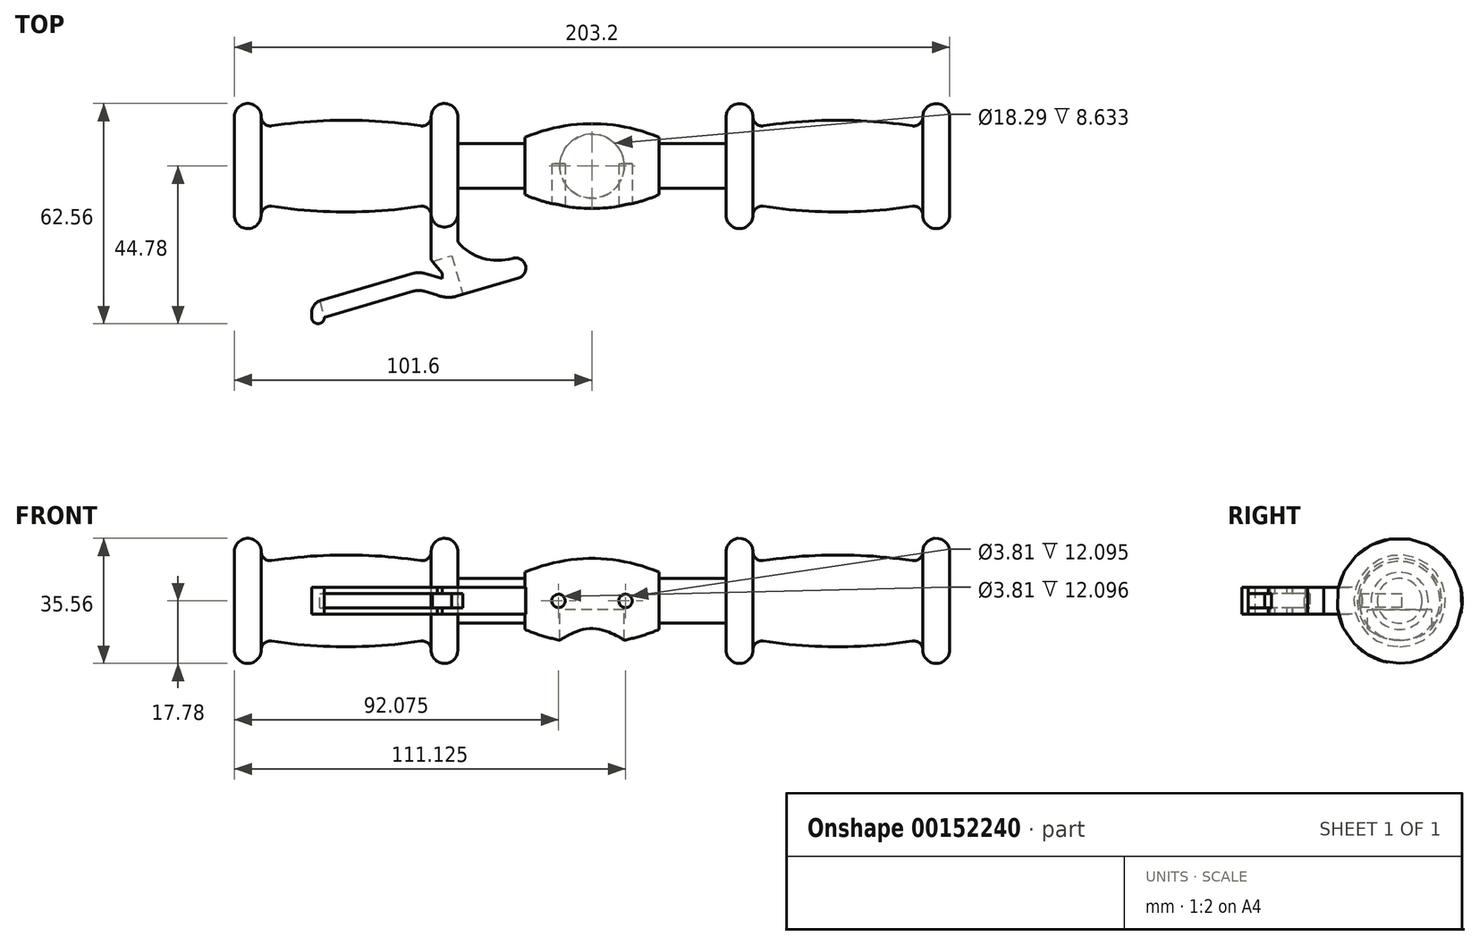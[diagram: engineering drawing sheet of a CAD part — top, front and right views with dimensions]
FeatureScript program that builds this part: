
annotation { "Feature Type Name" : "Feature", "Feature Type Description" : "" }
export const myFeature = defineFeature(function(context is Context, id is Id, definition is map)
    precondition{}
    {
        {
            var Q0;
            Q0=qCreatedBy(makeId("Right.planeOp"),FACE);
            var sketch = newSketch(context, id + "F0", { "sketchPlane" : qUnion([Q0])});
            skCircle(sketch, "E0", {"center": v(0, 0) * mm, "radius": 6.35 * mm});
            skSolve(sketch);
        }
        {
            var Q0;
            Q0 = qSketchRegion(id + "F0", true);
            extrude(context, id + "F1", {"entities" : qUnion([Q0]), "depth" : 203.2 * mm});
        }
        {
            var Q0;
            Q0=qCreatedBy(makeId("Front.planeOp"),FACE);
            var sketch = newSketch(context, id + "F2", { "sketchPlane" : qUnion([Q0])});
            skLineSegment(sketch, "E1", {"start": v(0, 6.35) * mm, "end": v(203.2, 6.35) * mm, "construction": true});
            skLineSegment(sketch, "E2", {"start": v(139.7, 6.35) * mm, "end": v(139.7, 13.97) * mm});
            skArc(sketch, "E3", {"start": v(147.32, 13.97) * mm, "mid": v(143.51, 17.78) * mm, "end": v(139.7, 13.97) * mm});
            skArc(sketch, "E4", {"start": v(147.32, 13.97) * mm, "mid": v(148.22, 12.02) * mm, "end": v(150.28, 11.43) * mm});
            skLineSegment(sketch, "E5", {"start": v(203.2, 6.35) * mm, "end": v(203.2, 13.97) * mm});
            skArc(sketch, "E6", {"start": v(203.2, 13.97) * mm, "mid": v(199.4, 17.78) * mm, "end": v(195.58, 13.97) * mm});
            skArc(sketch, "E7", {"start": v(195.58, 13.97) * mm, "mid": v(194.68, 12.02) * mm, "end": v(192.62, 11.43) * mm});
            skLineSegment(sketch, "E8", {"start": v(139.7, 6.35) * mm, "end": v(203.2, 6.35) * mm});
            skArc(sketch, "E9", {"start": v(192.62, 11.43) * mm, "mid": v(171.45, 13.04) * mm, "end": v(150.28, 11.43) * mm});
            skLineSegment(sketch, "E10", {"start": v(0, 6.35) * mm, "end": v(0, 13.97) * mm});
            skArc(sketch, "E11", {"start": v(7.62, 13.97) * mm, "mid": v(3.81, 17.78) * mm, "end": v(0, 13.97) * mm});
            skArc(sketch, "E12", {"start": v(7.62, 13.97) * mm, "mid": v(8.52, 12.02) * mm, "end": v(10.58, 11.43) * mm});
            skLineSegment(sketch, "E13", {"start": v(63.5, 6.35) * mm, "end": v(63.5, 13.97) * mm});
            skArc(sketch, "E14", {"start": v(63.5, 13.97) * mm, "mid": v(59.7, 17.78) * mm, "end": v(55.88, 13.97) * mm});
            skArc(sketch, "E15", {"start": v(55.88, 13.97) * mm, "mid": v(54.98, 12.02) * mm, "end": v(52.92, 11.43) * mm});
            skLineSegment(sketch, "E16", {"start": v(0, 6.35) * mm, "end": v(78.18, 6.35) * mm});
            skArc(sketch, "E17", {"start": v(52.92, 11.43) * mm, "mid": v(31.75, 13.04) * mm, "end": v(10.58, 11.43) * mm});
            skPoint(sketch, "E18", {"position": v(0, 6.35) * mm});
            skPoint(sketch, "E19", {"position": v(143.51, 17.78) * mm});
            skSolve(sketch);
        }
        {
            var Q0;
            Q0 = qSketchRegion(id + "F2", true);
            var Q1;
            Q1=makeQuery(id+"F1.opExtrude","SWEPT_FACE",FACE,{"disambiguationData":[OSD([sQuery(id+"F0.wireOp",EDGE,"E0")])]});
            revolve(context, id + "F3", {"operationType" : NewBodyOperationType.ADD, "entities" : qUnion([Q0]), "axis" : qUnion([Q1]), "revolveType" : RevolveType.FULL});
        }
        {
            var Q0;
            Q0=qCreatedBy(makeId("Front.planeOp"),FACE);
            var sketch = newSketch(context, id + "F4", { "sketchPlane" : qUnion([Q0])});
            skLineSegment(sketch, "E20", {"start": v(63.5, 6.35) * mm, "end": v(139.7, 6.35) * mm, "construction": true});
            skLineSegment(sketch, "E21", {"start": v(82.55, 6.35) * mm, "end": v(82.55, 8.13) * mm});
            skLineSegment(sketch, "E22", {"start": v(120.65, 6.35) * mm, "end": v(120.65, 8.13) * mm});
            skLineSegment(sketch, "E23", {"start": v(82.55, 6.35) * mm, "end": v(120.65, 6.35) * mm});
            skLineSegment(sketch, "E24", {"start": v(63.5, 13.97) * mm, "end": v(63.5, -13.97) * mm, "construction": true});
            skLineSegment(sketch, "E25.0", {"start": v(139.7, 13.97) * mm, "end": v(139.7, -13.97) * mm, "construction": true});
            skArc(sketch, "E26", {"start": v(120.65, 8.13) * mm, "mid": v(101.6, 12.05) * mm, "end": v(82.55, 8.13) * mm});
            skPoint(sketch, "E27", {"position": v(101.6, 12.05) * mm});
            skSolve(sketch);
        }
        {
            var Q0;
            Q0 = qSketchRegion(id + "F4", true);
            var Q1;
            Q1=makeQuery(id+"F1.opExtrude","SWEPT_FACE",FACE,{"disambiguationData":[OSD([sQuery(id+"F0.wireOp",EDGE,"E0")])]});
            revolve(context, id + "F5", {"operationType" : NewBodyOperationType.ADD, "entities" : qUnion([Q0]), "axis" : qUnion([Q1]), "revolveType" : RevolveType.FULL});
        }
        {
            var Q0;
            Q0=qCreatedBy(makeId("Top.planeOp"),FACE);
            var sketch = newSketch(context, id + "F6", { "sketchPlane" : qUnion([Q0])});
            skLineSegment(sketch, "E28.0", {"start": v(120.65, 8.13) * mm, "end": v(120.65, -8.13) * mm, "construction": true});
            skLineSegment(sketch, "E29.0", {"start": v(82.55, 8.13) * mm, "end": v(82.55, -8.13) * mm, "construction": true});
            skLineSegment(sketch, "E30", {"start": v(82.55, 0) * mm, "end": v(120.65, 0) * mm, "construction": true});
            skArc(sketch, "E31", {"start": v(82.55, -8.13) * mm, "mid": v(101.6, -12.05) * mm, "end": v(120.65, -8.13) * mm, "construction": true});
            skPoint(sketch, "E32", {"position": v(101.6, -12.05) * mm});
            skSolve(sketch);
        }
        {
            var Q0;
            Q0=sQuery(id+"F6.wireOp",VERTEX,"E32");
            var Q1;
            Q1=qCreatedBy(makeId("Front.planeOp"),FACE);
            cPlane(context, id + "F7", {"entities" : qUnion([Q0, Q1]), "cplaneType" : CPlaneType.PLANE_POINT, "offset" : 25.4 * mm, "width" : 152.4 * mm, "height" : 152.4 * mm});
        }
        {
            var Q0;
            Q0=qCreatedBy(id+"F7.planeOp",FACE);
            var sketch = newSketch(context, id + "F8", { "sketchPlane" : qUnion([Q0])});
            skLineSegment(sketch, "E33.0", {"start": v(82.55, 8.13) * mm, "end": v(82.55, -8.13) * mm, "construction": true});
            skLineSegment(sketch, "E34.0", {"start": v(120.65, 8.13) * mm, "end": v(120.65, -8.13) * mm, "construction": true});
            skLineSegment(sketch, "E35.0", {"start": v(82.55, 0) * mm, "end": v(120.65, 0) * mm, "construction": true});
            skCircle(sketch, "E36", {"center": v(92.08, 0) * mm, "radius": 1.9 * mm});
            skCircle(sketch, "E37", {"center": v(111.13, 0) * mm, "radius": 1.9 * mm});
            skSolve(sketch);
        }
        {
            var Q0;
            Q0 = qSketchRegion(id + "F8", true);
            extrude(context, id + "F9", {"entities" : qUnion([Q0]), "operationType" : NewBodyOperationType.REMOVE, "oppositeDirection" : true, "depth" : 12.7 * mm});
        }
        {
            var Q0;
            Q0=qCreatedBy(makeId("Right.planeOp"),FACE);
            var sketch = newSketch(context, id + "F10", { "sketchPlane" : qUnion([Q0])});
            skCircle(sketch, "E38", {"center": v(0, 0) * mm, "radius": 17.78 * mm, "construction": true});
            skLineSegment(sketch, "E39", {"start": v(0, 0) * mm, "end": v(-17.78, 0) * mm, "construction": true});
            skPoint(sketch, "E40", {"position": v(-17.78, 0) * mm});
            skSolve(sketch);
        }
        {
            var Q0;
            Q0=sQuery(id+"F10.wireOp",VERTEX,"E40");
            var Q1;
            Q1=qCreatedBy(makeId("Front.planeOp"),FACE);
            cPlane(context, id + "F11", {"entities" : qUnion([Q0, Q1]), "cplaneType" : CPlaneType.PLANE_POINT, "offset" : 25.4 * mm, "width" : 152.4 * mm, "height" : 152.4 * mm});
        }
        {
            var Q0;
            Q0=qCreatedBy(id+"F11.planeOp",FACE);
            var sketch = newSketch(context, id + "F12", { "sketchPlane" : qUnion([Q0])});
            skLineSegment(sketch, "E41", {"start": v(63.5, 13.97) * mm, "end": v(63.5, -13.97) * mm, "construction": true});
            skLineSegment(sketch, "E42", {"start": v(55.88, 13.97) * mm, "end": v(55.88, -13.97) * mm, "construction": true});
            skLineSegment(sketch, "E43.bottom", {"start": v(55.88, 3.81) * mm, "end": v(63.5, 3.81) * mm});
            skLineSegment(sketch, "E43.top", {"start": v(55.88, -3.81) * mm, "end": v(63.5, -3.81) * mm});
            skLineSegment(sketch, "E43.left", {"start": v(55.88, 3.81) * mm, "end": v(55.88, -3.81) * mm});
            skLineSegment(sketch, "E43.right", {"start": v(63.5, 3.8) * mm, "end": v(63.5, -3.81) * mm});
            skSolve(sketch);
        }
        {
            var Q0;
            Q0 = qSketchRegion(id + "F12", true);
            extrude(context, id + "F13", {"entities" : qUnion([Q0]), "operationType" : NewBodyOperationType.ADD, "depth" : 3.8 * mm, "hasSecondDirection" : true, "secondDirectionOppositeDirection" : true, "secondDirectionDepth" : 4.44 * mm});
        }
        {
            var Q0;
            Q0=makeQuery(id+"F13.opExtrude","SWEPT_FACE",FACE,{"disambiguationData":[OSD([sQuery(id+"F12.wireOp",EDGE,"E43.bottom")])]});
            var sketch = newSketch(context, id + "F14", { "sketchPlane" : qUnion([Q0])});
            skArc(sketch, "E44", {"start": v(63.5, -21.59) * mm, "mid": v(70.6, -26.2) * mm, "end": v(79.06, -26.2) * mm});
            skLineSegment(sketch, "E45", {"start": v(55.88, -21.6) * mm, "end": v(55.88, -26.67) * mm});
            skLineSegment(sketch, "E46", {"start": v(55.88, -26.67) * mm, "end": v(59, -30.48) * mm});
            skLineSegment(sketch, "E47", {"start": v(59, -30.48) * mm, "end": v(59, -31.98) * mm});
            skLineSegment(sketch, "E48", {"start": v(59, -31.98) * mm, "end": v(53.88, -30.48) * mm});
            skArc(sketch, "E49", {"start": v(53.88, -30.48) * mm, "mid": v(52.39, -30.27) * mm, "end": v(50.9, -30.48) * mm});
            skLineSegment(sketch, "E50", {"start": v(50.9, -30.48) * mm, "end": v(24.55, -38.2) * mm});
            skArc(sketch, "E51", {"start": v(24.55, -38.2) * mm, "mid": v(22.87, -39.26) * mm, "end": v(21.99, -41.03) * mm});
            skLineSegment(sketch, "E52", {"start": v(21.99, -41.03) * mm, "end": v(21.99, -42.99) * mm});
            skLineSegment(sketch, "E53", {"start": v(25.58, -42.99) * mm, "end": v(50.9, -35.56) * mm});
            skArc(sketch, "E54", {"start": v(50.9, -35.56) * mm, "mid": v(52.39, -35.35) * mm, "end": v(53.88, -35.56) * mm});
            skLineSegment(sketch, "E55", {"start": v(53.88, -35.56) * mm, "end": v(59, -37.06) * mm});
            skArc(sketch, "E56", {"start": v(59, -37.06) * mm, "mid": v(60.9, -37.33) * mm, "end": v(62.81, -37.06) * mm});
            skLineSegment(sketch, "E57", {"start": v(62.81, -37.06) * mm, "end": v(80.7, -31.81) * mm});
            skArc(sketch, "E58", {"start": v(80.7, -31.81) * mm, "mid": v(82.68, -28.19) * mm, "end": v(79.06, -26.2) * mm});
            skArc(sketch, "E59", {"start": v(21.99, -42.99) * mm, "mid": v(23.78, -44.78) * mm, "end": v(25.58, -42.99) * mm});
            skLineSegment(sketch, "E60", {"start": v(55.88, -21.6) * mm, "end": v(63.5, -21.6) * mm});
            skCircle(sketch, "E61", {"center": v(59, -34.52) * mm, "radius": 2.54 * mm});
            skSolve(sketch);
        }
        {
            var Q0;
            Q0 = qSketchRegion(id + "F14", true);
            extrude(context, id + "F15", {"entities" : qUnion([Q0]), "operationType" : NewBodyOperationType.ADD, "oppositeDirection" : true, "depth" : 7.62 * mm});
        }
        {
            var Q0;
            Q0=makeQuery(id+"F15.opExtrude","SWEPT_FACE",FACE,{"disambiguationData":[OSD([sQuery(id+"F14.wireOp",EDGE,"E57")])]});
            var sketch = newSketch(context, id + "F16", { "sketchPlane" : qUnion([Q0])});
            skLineSegment(sketch, "E62.bottom", {"start": v(12.44, 2.03) * mm, "end": v(52.07, 2.03) * mm});
            skLineSegment(sketch, "E62.top", {"start": v(12.44, -2.03) * mm, "end": v(52.07, -2.03) * mm});
            skLineSegment(sketch, "E62.left", {"start": v(12.44, 2.03) * mm, "end": v(12.44, -2.03) * mm});
            skLineSegment(sketch, "E62.right", {"start": v(52.07, 2.03) * mm, "end": v(52.07, -2.03) * mm});
            skSolve(sketch);
        }
        {
            var Q0;
            Q0 = qSketchRegion(id + "F16", true);
            extrude(context, id + "F17", {"entities" : qUnion([Q0]), "operationType" : NewBodyOperationType.REMOVE, "oppositeDirection" : true, "depth" : 11.43 * mm});
        }
        {
            var Q0;
            Q0=qCreatedBy(makeId("Top.planeOp"),FACE);
            var sketch = newSketch(context, id + "F18", { "sketchPlane" : qUnion([Q0])});
            skCircle(sketch, "E63", {"center": v(101.6, 0) * mm, "radius": 9.14 * mm});
            skSolve(sketch);
        }
        {
            var Q0;
            Q0 = qSketchRegion(id + "F18", true);
            extrude(context, id + "F19", {"entities" : qUnion([Q0]), "operationType" : NewBodyOperationType.REMOVE, "oppositeDirection" : true, "depth" : 25.4 * mm, "hasSecondDirection" : true, "secondDirectionOppositeDirection" : true, "secondDirectionDepth" : 2.54 * mm});
        }
    });
